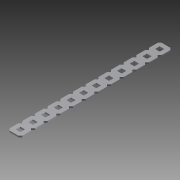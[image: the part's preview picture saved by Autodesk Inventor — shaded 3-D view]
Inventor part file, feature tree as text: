
AUTODESK INVENTOR PART (.ipt)
format: ipt  version: 2014 SP1 (Build 180222100, 222)  size: 524,288 bytes
history: native  units: in
note: dims shown in document units (in); Inventor stores cm internally (conversion verified against a paired STEP export)
features: other x1, imported_body x1, extrude x1, sketch x1
ambient origin geometry x8: Origin, YZ Plane, XZ Plane, XY Plane, X Axis, Y Axis, Z Axis, Center Point
bodies: Body1 (feature_tree)
feature tree (4):
  parser-record x1  (decoder bookkeeping rows leaked as tree rows — omitted from the tree; the rows remain in map.json)
  imported_body  "Base1"
  extrude  "Extrusion1"  Depth=1.0in TaperAngle=0.0deg
  sketch  "Sketch1"  dims[d0=6.0in d1=1.0in d2=0.0in]
